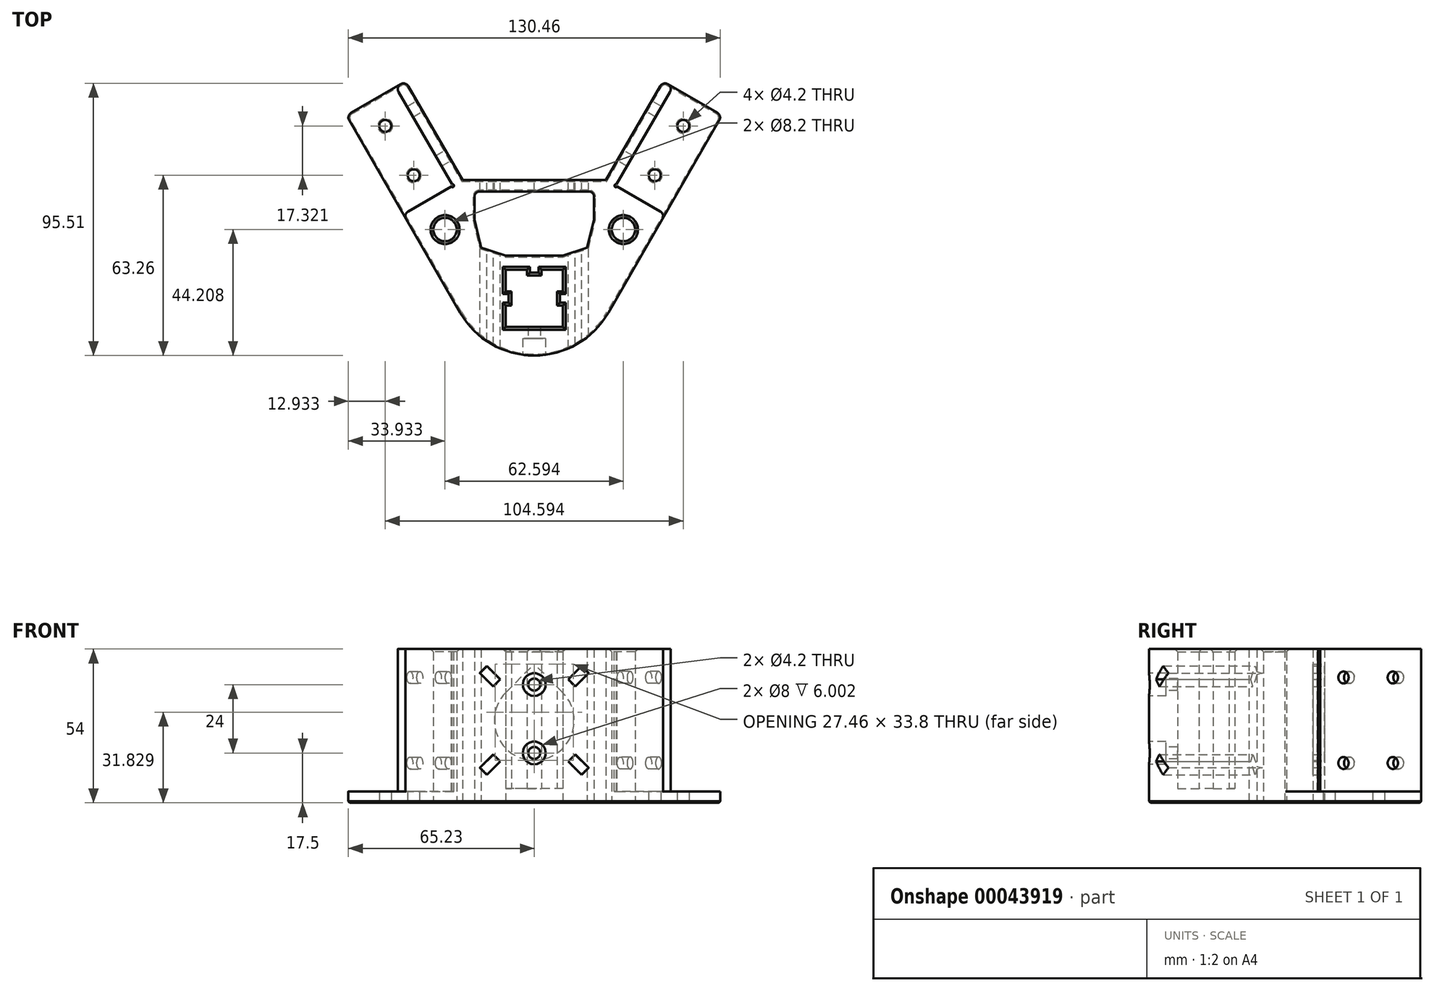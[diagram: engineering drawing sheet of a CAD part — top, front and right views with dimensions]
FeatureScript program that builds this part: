
annotation { "Feature Type Name" : "Feature", "Feature Type Description" : "" }
export const myFeature = defineFeature(function(context is Context, id is Id, definition is map)
    precondition{}
    {
        {
            var Q0;
            Q0=qCreatedBy(makeId("Top.planeOp"),FACE);
            var sketch = newSketch(context, id + "F0", { "sketchPlane" : qUnion([Q0])});
            skLineSegment(sketch, "E0.rect.bottom", {"start": v(10.05, -10.05) * mm, "end": v(-10.05, -10.05) * mm});
            skLineSegment(sketch, "E0.rect.top", {"start": v(10.05, 10.05) * mm, "end": v(-10.05, 10.05) * mm});
            skLineSegment(sketch, "E0.rect.left", {"start": v(10.05, -10.05) * mm, "end": v(10.05, 10.05) * mm});
            skLineSegment(sketch, "E0.rect.right", {"start": v(-10.05, -10.05) * mm, "end": v(-10.05, 10.05) * mm});
            skPoint(sketch, "E0.rect.middle", {"position": v(0, 0) * mm});
            skLineSegment(sketch, "E1", {"start": v(-10.05, -2.5) * mm, "end": v(-8.05, -2.5) * mm});
            skLineSegment(sketch, "E2", {"start": v(-8.05, -2.5) * mm, "end": v(-8.05, 2.5) * mm});
            skLineSegment(sketch, "E3", {"start": v(-8.05, 2.5) * mm, "end": v(-10.05, 2.5) * mm});
            skLineSegment(sketch, "E4", {"start": v(-2.5, 10.05) * mm, "end": v(-2.5, 8.05) * mm});
            skLineSegment(sketch, "E5", {"start": v(-2.5, 8.05) * mm, "end": v(2.5, 8.05) * mm});
            skLineSegment(sketch, "E6", {"start": v(2.5, 8.05) * mm, "end": v(2.5, 10.05) * mm});
            skLineSegment(sketch, "E7", {"start": v(10.05, 2.5) * mm, "end": v(8.05, 2.5) * mm});
            skLineSegment(sketch, "E8", {"start": v(8.05, 2.5) * mm, "end": v(8.05, -2.5) * mm});
            skLineSegment(sketch, "E9", {"start": v(8.05, -2.5) * mm, "end": v(10.05, -2.5) * mm});
            skLineSegment(sketch, "E10", {"start": v(-25.98, -5.05) * mm, "end": v(-65.96, 64.2) * mm});
            skLineSegment(sketch, "E11", {"start": v(-65.96, 64.2) * mm, "end": v(-45.17, 76.2) * mm});
            skLineSegment(sketch, "E12", {"start": v(-45.17, 76.2) * mm, "end": v(-25.17, 41.55) * mm});
            skLineSegment(sketch, "E13", {"start": v(-25.17, 41.55) * mm, "end": v(25.17, 41.55) * mm});
            skLineSegment(sketch, "E14", {"start": v(25.17, 41.55) * mm, "end": v(45.17, 76.2) * mm});
            skLineSegment(sketch, "E15", {"start": v(45.17, 76.2) * mm, "end": v(65.96, 64.2) * mm});
            skLineSegment(sketch, "E16", {"start": v(65.96, 64.2) * mm, "end": v(25.98, -5.05) * mm});
            skPoint(sketch, "E17.visualSharp", {"position": v(0, -50.05) * mm});
            skArc(sketch, "E17.filletArc", {"start": v(-25.98, -5.05) * mm, "mid": v(0, -20.05) * mm, "end": v(25.98, -5.05) * mm});
            skLineSegment(sketch, "E18", {"start": v(-48.64, 74.2) * mm, "end": v(-28.64, 39.55) * mm});
            skLineSegment(sketch, "E19", {"start": v(-28.64, 39.55) * mm, "end": v(-45.96, 29.55) * mm});
            skLineSegment(sketch, "E20", {"start": v(48.64, 74.2) * mm, "end": v(28.64, 39.55) * mm});
            skLineSegment(sketch, "E21", {"start": v(28.64, 39.55) * mm, "end": v(45.96, 29.55) * mm});
            skLineSegment(sketch, "E22", {"start": v(-28.64, 39.55) * mm, "end": v(-25.17, 41.55) * mm, "construction": true});
            skLineSegment(sketch, "E23", {"start": v(-57.3, 69.2) * mm, "end": v(-37.3, 34.55) * mm, "construction": true});
            skCircle(sketch, "E24", {"center": v(-52.3, 60.53) * mm, "radius": 2.1 * mm});
            skCircle(sketch, "E25", {"center": v(-42.3, 43.21) * mm, "radius": 2.1 * mm});
            skCircle(sketch, "E26", {"center": v(52.3, 60.53) * mm, "radius": 2.1 * mm});
            skCircle(sketch, "E27", {"center": v(42.3, 43.21) * mm, "radius": 2.1 * mm});
            skLineSegment(sketch, "E28", {"start": v(-21, 37.55) * mm, "end": v(21, 37.55) * mm});
            skLineSegment(sketch, "E29", {"start": v(21, 37.55) * mm, "end": v(21, 27.55) * mm});
            skLineSegment(sketch, "E30", {"start": v(10.05, 15.05) * mm, "end": v(-10.05, 15.05) * mm});
            skLineSegment(sketch, "E31", {"start": v(-21, 27.55) * mm, "end": v(-21, 37.55) * mm});
            skLineSegment(sketch, "E32", {"start": v(-21, 27.55) * mm, "end": v(-18.6, 17.84) * mm});
            skLineSegment(sketch, "E33", {"start": v(-18.6, 17.84) * mm, "end": v(-10.05, 15.05) * mm});
            skLineSegment(sketch, "E34", {"start": v(21, 27.55) * mm, "end": v(18.6, 17.84) * mm});
            skLineSegment(sketch, "E35", {"start": v(18.6, 17.84) * mm, "end": v(10.05, 15.05) * mm});
            skLineSegment(sketch, "E36", {"start": v(-37.3, 34.55) * mm, "end": v(-20.56, 5.56) * mm, "construction": true});
            skCircle(sketch, "E37", {"center": v(-31.3, 24.16) * mm, "radius": 4.1 * mm});
            skLineSegment(sketch, "E38", {"start": v(0, -71.13) * mm, "end": v(0, 233.1) * mm, "construction": true});
            skCircle(sketch, "E39", {"center": v(31.3, 24.16) * mm, "radius": 4.1 * mm});
            skSolve(sketch);
        }
        {
            var Q0;
            {var subQ5=sQuery(id+"F0.wireOp",EDGE,"E0.rect.bottom");Q0=makeQuery(id+"F0.imprint","IMPRINT",FACE,{"disambiguationData":[TD([[makeQuery(id+"F0.imprint","IMPRINT",EDGE,{"derivedFrom":subQ5}),1.0]])]});}
            var Q1;
            {var subQ1=sQuery(id+"F0.wireOp",EDGE,"E18");Q1=makeQuery(id+"F0.imprint","IMPRINT",FACE,{"disambiguationData":[TD([[makeQuery(id+"F0.imprint","IMPRINT",EDGE,{"derivedFrom":subQ1}),-1.0]])]});}
            var Q2;
            {var subQ0=sQuery(id+"F0.wireOp",EDGE,"E20");Q2=makeQuery(id+"F0.imprint","IMPRINT",FACE,{"disambiguationData":[TD([[makeQuery(id+"F0.imprint","IMPRINT",EDGE,{"derivedFrom":subQ0}),1.0]])]});}
            var Q3;
            {var subQ1=sQuery(id+"F0.wireOp",EDGE,"E1");Q3=makeQuery(id+"F0.imprint","IMPRINT",FACE,{"disambiguationData":[TD([[makeQuery(id+"F0.imprint","IMPRINT",EDGE,{"derivedFrom":subQ1}),1.0]])]});}
            var Q4;
            {var subQ1=sQuery(id+"F0.wireOp",EDGE,"E4");Q4=makeQuery(id+"F0.imprint","IMPRINT",FACE,{"disambiguationData":[TD([[makeQuery(id+"F0.imprint","IMPRINT",EDGE,{"derivedFrom":subQ1}),1.0]])]});}
            var Q5;
            {var subQ1=sQuery(id+"F0.wireOp",EDGE,"E7");Q5=makeQuery(id+"F0.imprint","IMPRINT",FACE,{"disambiguationData":[TD([[makeQuery(id+"F0.imprint","IMPRINT",EDGE,{"derivedFrom":subQ1}),1.0]])]});}
            extrude(context, id + "F1", {"entities" : qUnion([Q0, Q1, Q2, Q3, Q4, Q5]), "depth" : 4 * mm});
        }
        {
            var Q0;
            Q0=makeQuery(id+"F1.opExtrude","CAP_FACE",FACE,{"disambiguationData":[OSD([sQuery(id+"F0.wireOp",EDGE,"E0.rect.bottom"),sQuery(id+"F0.wireOp",EDGE,"E0.rect.top"),sQuery(id+"F0.wireOp",EDGE,"E0.rect.left"),sQuery(id+"F0.wireOp",EDGE,"E0.rect.right"),sQuery(id+"F0.wireOp",EDGE,"E1"),sQuery(id+"F0.wireOp",EDGE,"E2"),sQuery(id+"F0.wireOp",EDGE,"E3"),sQuery(id+"F0.wireOp",EDGE,"E4"),sQuery(id+"F0.wireOp",EDGE,"E5"),sQuery(id+"F0.wireOp",EDGE,"E6"),sQuery(id+"F0.wireOp",EDGE,"E7"),sQuery(id+"F0.wireOp",EDGE,"E8"),sQuery(id+"F0.wireOp",EDGE,"E9"),sQuery(id+"F0.wireOp",EDGE,"E10"),sQuery(id+"F0.wireOp",EDGE,"E11"),sQuery(id+"F0.wireOp",EDGE,"E12"),sQuery(id+"F0.wireOp",EDGE,"E13"),sQuery(id+"F0.wireOp",EDGE,"E14"),sQuery(id+"F0.wireOp",EDGE,"E15"),sQuery(id+"F0.wireOp",EDGE,"E16"),sQuery(id+"F0.wireOp",EDGE,"E17.filletArc"),sQuery(id+"F0.wireOp",EDGE,"E24"),sQuery(id+"F0.wireOp",EDGE,"E25"),sQuery(id+"F0.wireOp",EDGE,"E26"),sQuery(id+"F0.wireOp",EDGE,"E27"),sQuery(id+"F0.wireOp",EDGE,"E28"),sQuery(id+"F0.wireOp",EDGE,"E29"),sQuery(id+"F0.wireOp",EDGE,"E30"),sQuery(id+"F0.wireOp",EDGE,"E31"),sQuery(id+"F0.wireOp",EDGE,"E32"),sQuery(id+"F0.wireOp",EDGE,"E33"),sQuery(id+"F0.wireOp",EDGE,"E34"),sQuery(id+"F0.wireOp",EDGE,"E35"),sQuery(id+"F0.wireOp",EDGE,"E37"),sQuery(id+"F0.wireOp",EDGE,"E39")])],"isStart":false});
            var sketch = newSketch(context, id + "F2", { "sketchPlane" : qUnion([Q0])});
            skLineSegment(sketch, "E40.0", {"start": v(-48.64, 74.2) * mm, "end": v(-28.64, 39.55) * mm});
            skLineSegment(sketch, "E41.0", {"start": v(-28.64, 39.55) * mm, "end": v(-45.96, 29.55) * mm});
            skLineSegment(sketch, "E42.0", {"start": v(48.64, 74.2) * mm, "end": v(28.64, 39.55) * mm});
            skLineSegment(sketch, "E43.0", {"start": v(28.64, 39.55) * mm, "end": v(45.96, 29.55) * mm});
            skSolve(sketch);
        }
        {
            var Q0;
            {var subQ7=sQuery(id+"F2.wireOp",EDGE,"E40.0");Q0=makeQuery(id+"F2.imprint","IMPRINT",FACE,{"disambiguationData":[TD([[makeQuery(id+"F2.imprint","IMPRINT",EDGE,{"derivedFrom":subQ7}),1.0]])]});}
            extrude(context, id + "F3", {"entities" : qUnion([Q0]), "operationType" : NewBodyOperationType.ADD, "depth" : 50 * mm});
        }
        {
            var Q0;
            {var subQ0=sQuery(id+"F0.wireOp",EDGE,"E13");Q0=makeQuery(id+"F3.boolean.opBoolean","MERGE",FACE,{"derivedFrom":[makeQuery(id+"F1.opExtrude","SWEPT_FACE",FACE,{"disambiguationData":[OSD([subQ0])]}),makeQuery(id+"F3.opExtrude","SWEPT_FACE",FACE,{"disambiguationData":[OSD([subQ0])]})]});}
            var sketch = newSketch(context, id + "F4", { "sketchPlane" : qUnion([Q0])});
            skCircle(sketch, "E44", {"center": v(0, 28.93) * mm, "radius": 14 * mm});
            skLineSegment(sketch, "E45", {"start": v(0, 28.93) * mm, "end": v(-14.76, 43.7) * mm, "construction": true});
            skLineSegment(sketch, "E46", {"start": v(-19.07, 45.53) * mm, "end": v(-16.6, 48) * mm});
            skLineSegment(sketch, "E47", {"start": v(-16.6, 48) * mm, "end": v(-11.93, 43.33) * mm});
            skLineSegment(sketch, "E48", {"start": v(-11.93, 43.33) * mm, "end": v(-14.4, 40.86) * mm});
            skLineSegment(sketch, "E49", {"start": v(-14.4, 40.86) * mm, "end": v(-19.07, 45.53) * mm});
            skLineSegment(sketch, "E50.1.0", {"start": v(-11.93, 14.53) * mm, "end": v(-16.6, 9.86) * mm});
            skLineSegment(sketch, "E50.1.1", {"start": v(-16.6, 9.86) * mm, "end": v(-19.07, 12.33) * mm});
            skLineSegment(sketch, "E50.1.2", {"start": v(-19.07, 12.33) * mm, "end": v(-14.4, 17) * mm});
            skLineSegment(sketch, "E50.1.3", {"start": v(-14.4, 17) * mm, "end": v(-11.93, 14.53) * mm});
            skLineSegment(sketch, "E50.2.0", {"start": v(14.4, 17) * mm, "end": v(19.07, 12.33) * mm});
            skLineSegment(sketch, "E50.2.1", {"start": v(19.07, 12.33) * mm, "end": v(16.6, 9.86) * mm});
            skLineSegment(sketch, "E50.2.2", {"start": v(16.6, 9.86) * mm, "end": v(11.93, 14.53) * mm});
            skLineSegment(sketch, "E50.2.3", {"start": v(11.93, 14.53) * mm, "end": v(14.4, 17) * mm});
            skLineSegment(sketch, "E50.3.0", {"start": v(11.93, 43.33) * mm, "end": v(16.6, 48) * mm});
            skLineSegment(sketch, "E50.3.1", {"start": v(16.6, 48) * mm, "end": v(19.07, 45.53) * mm});
            skLineSegment(sketch, "E50.3.2", {"start": v(19.07, 45.53) * mm, "end": v(14.4, 40.86) * mm});
            skLineSegment(sketch, "E50.3.3", {"start": v(14.4, 40.86) * mm, "end": v(11.93, 43.33) * mm});
            skLineSegment(sketch, "E51", {"start": v(0, 48.73) * mm, "end": v(-9.9, 38.83) * mm});
            skLineSegment(sketch, "E52", {"start": v(0, 48.73) * mm, "end": v(9.9, 38.83) * mm});
            skSolve(sketch);
        }
        {
            var Q0;
            Q0=makeQuery(id+"F4.imprint","IMPRINT",FACE,{"disambiguationData":[TD([[makeQuery(id+"F4.imprint","IMPRINT",EDGE,{"derivedFrom":sQuery(id+"F4.wireOp",EDGE,"E44")}),1.0]])]});
            var Q1;
            {var subQ1=sQuery(id+"F4.wireOp",EDGE,"E51");Q1=makeQuery(id+"F4.imprint","IMPRINT",FACE,{"disambiguationData":[TD([[makeQuery(id+"F4.imprint","IMPRINT",EDGE,{"derivedFrom":subQ1}),1.0]])]});}
            extrude(context, id + "F5", {"entities" : qUnion([Q0, Q1]), "operationType" : NewBodyOperationType.REMOVE, "endBound" : BoundingType.UP_TO_NEXT, "oppositeDirection" : true, "depth" : 25 * mm});
        }
        {
            var Q0;
            Q0=makeQuery(id+"F4.imprint","IMPRINT",FACE,{"disambiguationData":[TD([[makeQuery(id+"F4.imprint","IMPRINT",EDGE,{"derivedFrom":sQuery(id+"F4.wireOp",EDGE,"E46")}),-1.0]])]});
            var Q1;
            Q1=makeQuery(id+"F4.imprint","IMPRINT",FACE,{"disambiguationData":[TD([[makeQuery(id+"F4.imprint","IMPRINT",EDGE,{"derivedFrom":sQuery(id+"F4.wireOp",EDGE,"E50.3.0")}),-1.0]])]});
            var Q2;
            Q2=makeQuery(id+"F4.imprint","IMPRINT",FACE,{"disambiguationData":[TD([[makeQuery(id+"F4.imprint","IMPRINT",EDGE,{"derivedFrom":sQuery(id+"F4.wireOp",EDGE,"E50.2.0")}),-1.0]])]});
            var Q3;
            Q3=makeQuery(id+"F4.imprint","IMPRINT",FACE,{"disambiguationData":[TD([[makeQuery(id+"F4.imprint","IMPRINT",EDGE,{"derivedFrom":sQuery(id+"F4.wireOp",EDGE,"E50.1.0")}),-1.0]])]});
            extrude(context, id + "F6", {"entities" : qUnion([Q0, Q1, Q2, Q3]), "operationType" : NewBodyOperationType.REMOVE, "endBound" : BoundingType.THROUGH_ALL, "oppositeDirection" : true, "depth" : 25 * mm});
        }
        {
            var Q0;
            {var subQ11=sQuery(id+"F0.wireOp",EDGE,"E0.rect.bottom");Q0=makeQuery(id+"F0.imprint","IMPRINT",FACE,{"disambiguationData":[TD([[makeQuery(id+"F0.imprint","IMPRINT",EDGE,{"derivedFrom":subQ11}),-1.0]])]});}
            extrude(context, id + "F7", {"entities" : qUnion([Q0]), "operationType" : NewBodyOperationType.ADD, "depth" : 5 * mm});
        }
        {
            var Q0;
            {var subQ0=sQuery(id+"F0.wireOp",EDGE,"E28");Q0=makeQuery(id+"F3.boolean.opBoolean","MERGE",FACE,{"derivedFrom":[makeQuery(id+"F1.opExtrude","SWEPT_FACE",FACE,{"disambiguationData":[OSD([subQ0])]}),makeQuery(id+"F3.opExtrude","SWEPT_FACE",FACE,{"disambiguationData":[OSD([subQ0])]})]});}
            cPlane(context, id + "F8", {"entities" : qUnion([Q0]), "cplaneType" : CPlaneType.OFFSET, "offset" : 100 * mm, "width" : 150 * mm, "height" : 150 * mm});
        }
        {
            var Q0;
            Q0=qCreatedBy(id+"F8.planeOp",FACE);
            var sketch = newSketch(context, id + "F9", { "sketchPlane" : qUnion([Q0])});
            skCircle(sketch, "E53", {"center": v(0, 41.5) * mm, "radius": 2.1 * mm});
            skCircle(sketch, "E54", {"center": v(0, 41.5) * mm, "radius": 4 * mm});
            skCircle(sketch, "E55", {"center": v(0, 17.5) * mm, "radius": 2.1 * mm});
            skCircle(sketch, "E56", {"center": v(0, 17.5) * mm, "radius": 4 * mm});
            skSolve(sketch);
        }
        {
            var Q0;
            Q0=makeQuery(id+"F9.imprint","IMPRINT",FACE,{"disambiguationData":[TD([[makeQuery(id+"F9.imprint","IMPRINT",EDGE,{"derivedFrom":sQuery(id+"F9.wireOp",EDGE,"E53")}),1.0]])]});
            var Q1;
            Q1=makeQuery(id+"F9.imprint","IMPRINT",FACE,{"disambiguationData":[TD([[makeQuery(id+"F9.imprint","IMPRINT",EDGE,{"derivedFrom":sQuery(id+"F9.wireOp",EDGE,"E55")}),1.0]])]});
            var Q2;
            {var subQ0=sQuery(id+"F0.wireOp",EDGE,"E0.rect.bottom");Q2=makeQuery(id+"F3.boolean.opBoolean","MERGE",FACE,{"derivedFrom":[makeQuery(id+"F1.opExtrude","SWEPT_FACE",FACE,{"disambiguationData":[OSD([subQ0])]}),makeQuery(id+"F3.opExtrude","SWEPT_FACE",FACE,{"disambiguationData":[OSD([subQ0])]})]});}
            extrude(context, id + "F10", {"entities" : qUnion([Q0, Q1]), "operationType" : NewBodyOperationType.REMOVE, "endBound" : BoundingType.UP_TO_SURFACE, "oppositeDirection" : true, "endBoundEntityFace" : qUnion([Q2]), "depth" : 25 * mm});
        }
        {
            var Q0;
            Q0=makeQuery(id+"F9.imprint","IMPRINT",FACE,{"disambiguationData":[TD([[makeQuery(id+"F9.imprint","IMPRINT",EDGE,{"derivedFrom":sQuery(id+"F9.wireOp",EDGE,"E53")}),-1.0]])]});
            var Q1;
            Q1=makeQuery(id+"F9.imprint","IMPRINT",FACE,{"disambiguationData":[TD([[makeQuery(id+"F9.imprint","IMPRINT",EDGE,{"derivedFrom":sQuery(id+"F9.wireOp",EDGE,"E55")}),-1.0]])]});
            extrude(context, id + "F11", {"entities" : qUnion([Q0, Q1]), "operationType" : NewBodyOperationType.REMOVE, "oppositeDirection" : true, "depth" : 48.4 * mm});
        }
        {
            var Q0;
            {var subQ0=sQuery(id+"F0.wireOp",EDGE,"E12");Q0=makeQuery(id+"F3.boolean.opBoolean","MERGE",FACE,{"derivedFrom":[makeQuery(id+"F1.opExtrude","SWEPT_FACE",FACE,{"disambiguationData":[OSD([subQ0])]}),makeQuery(id+"F3.opExtrude","SWEPT_FACE",FACE,{"disambiguationData":[OSD([subQ0])]})]});}
            var sketch = newSketch(context, id + "F12", { "sketchPlane" : qUnion([Q0])});
            skCircle(sketch, "E57", {"center": v(78.57, 44) * mm, "radius": 2.1 * mm});
            skCircle(sketch, "E58", {"center": v(58.57, 44) * mm, "radius": 2.1 * mm});
            skCircle(sketch, "E59", {"center": v(78.57, 14) * mm, "radius": 2.1 * mm});
            skCircle(sketch, "E60", {"center": v(58.57, 14) * mm, "radius": 2.1 * mm});
            skSolve(sketch);
        }
        {
            var Q0;
            Q0=qSketchRegion(id+"F12",true);
            extrude(context, id + "F13", {"entities" : qUnion([Q0]), "operationType" : NewBodyOperationType.REMOVE, "oppositeDirection" : true, "depth" : 25 * mm});
        }
        {
            var Q0;
            {var subQ0=sQuery(id+"F0.wireOp",EDGE,"E14");Q0=makeQuery(id+"F3.boolean.opBoolean","MERGE",FACE,{"derivedFrom":[makeQuery(id+"F1.opExtrude","SWEPT_FACE",FACE,{"disambiguationData":[OSD([subQ0])]}),makeQuery(id+"F3.opExtrude","SWEPT_FACE",FACE,{"disambiguationData":[OSD([subQ0])]})]});}
            var sketch = newSketch(context, id + "F14", { "sketchPlane" : qUnion([Q0])});
            skCircle(sketch, "E61", {"center": v(-78.57, 44) * mm, "radius": 2.1 * mm});
            skCircle(sketch, "E62", {"center": v(-58.57, 44) * mm, "radius": 2.1 * mm});
            skCircle(sketch, "E63", {"center": v(-78.57, 14) * mm, "radius": 2.1 * mm});
            skCircle(sketch, "E64", {"center": v(-58.57, 14) * mm, "radius": 2.1 * mm});
            skSolve(sketch);
        }
        {
            var Q0;
            Q0=qSketchRegion(id+"F14",true);
            extrude(context, id + "F15", {"entities" : qUnion([Q0]), "operationType" : NewBodyOperationType.REMOVE, "oppositeDirection" : true, "depth" : 25 * mm});
        }
        {
            var Q0;
            Q0=makeQuery(id+"F3.opExtrude","CAP_EDGE",EDGE,{"disambiguationData":[OSD([sQuery(id+"F0.wireOp",EDGE,"E0.rect.bottom")])],"isStart":false});
            var Q1;
            {var subQ0=sQuery(id+"F0.wireOp",EDGE,"E0.rect.left");Q1=makeQuery(id+"F3.opExtrude","CAP_EDGE",EDGE,{"disambiguationData":[OSD([subQ0]),TDD([makeQuery(id+"F2.imprint","IMPRINT",EDGE,{"derivedFrom":makeQuery(id+"F1.opExtrude","CAP_EDGE",EDGE,{"disambiguationData":[OSD([subQ0]),TDD([makeQuery(id+"F0.imprint","IMPRINT",EDGE,{"disambiguationData":[TD([[makeQuery(id+"F0.imprint","INTERSECT",VERTEX,{"derivedFrom":[sQuery(id+"F0.wireOp",EDGE,"E0.rect.bottom"),subQ0]}),-1.0]])],"derivedFrom":subQ0})])],"isStart":false})})])],"isStart":false});}
            var Q2;
            Q2=makeQuery(id+"F3.opExtrude","CAP_EDGE",EDGE,{"disambiguationData":[OSD([sQuery(id+"F0.wireOp",EDGE,"E9")])],"isStart":false});
            var Q3;
            Q3=makeQuery(id+"F3.opExtrude","CAP_EDGE",EDGE,{"disambiguationData":[OSD([sQuery(id+"F0.wireOp",EDGE,"E8")])],"isStart":false});
            var Q4;
            Q4=makeQuery(id+"F3.opExtrude","CAP_EDGE",EDGE,{"disambiguationData":[OSD([sQuery(id+"F0.wireOp",EDGE,"E7")])],"isStart":false});
            var Q5;
            {var subQ0=sQuery(id+"F0.wireOp",EDGE,"E0.rect.left");Q5=makeQuery(id+"F3.opExtrude","CAP_EDGE",EDGE,{"disambiguationData":[OSD([subQ0]),TDD([makeQuery(id+"F2.imprint","IMPRINT",EDGE,{"derivedFrom":makeQuery(id+"F1.opExtrude","CAP_EDGE",EDGE,{"disambiguationData":[OSD([subQ0]),TDD([makeQuery(id+"F0.imprint","IMPRINT",EDGE,{"disambiguationData":[TD([[makeQuery(id+"F0.imprint","INTERSECT",VERTEX,{"derivedFrom":[sQuery(id+"F0.wireOp",EDGE,"E0.rect.top"),subQ0]}),1.0]])],"derivedFrom":subQ0})])],"isStart":false})})])],"isStart":false});}
            var Q6;
            {var subQ0=sQuery(id+"F0.wireOp",EDGE,"E0.rect.top");Q6=makeQuery(id+"F3.opExtrude","CAP_EDGE",EDGE,{"disambiguationData":[OSD([subQ0]),TDD([makeQuery(id+"F2.imprint","IMPRINT",EDGE,{"derivedFrom":makeQuery(id+"F1.opExtrude","CAP_EDGE",EDGE,{"disambiguationData":[OSD([subQ0]),TDD([makeQuery(id+"F0.imprint","IMPRINT",EDGE,{"disambiguationData":[TD([[makeQuery(id+"F0.imprint","INTERSECT",VERTEX,{"derivedFrom":[subQ0,sQuery(id+"F0.wireOp",EDGE,"E0.rect.left")]}),-1.0]])],"derivedFrom":subQ0})])],"isStart":false})})])],"isStart":false});}
            var Q7;
            Q7=makeQuery(id+"F3.opExtrude","CAP_EDGE",EDGE,{"disambiguationData":[OSD([sQuery(id+"F0.wireOp",EDGE,"E6")])],"isStart":false});
            var Q8;
            Q8=makeQuery(id+"F3.opExtrude","CAP_EDGE",EDGE,{"disambiguationData":[OSD([sQuery(id+"F0.wireOp",EDGE,"E5")])],"isStart":false});
            var Q9;
            Q9=makeQuery(id+"F3.opExtrude","CAP_EDGE",EDGE,{"disambiguationData":[OSD([sQuery(id+"F0.wireOp",EDGE,"E4")])],"isStart":false});
            var Q10;
            {var subQ0=sQuery(id+"F0.wireOp",EDGE,"E0.rect.top");Q10=makeQuery(id+"F3.opExtrude","CAP_EDGE",EDGE,{"disambiguationData":[OSD([subQ0]),TDD([makeQuery(id+"F2.imprint","IMPRINT",EDGE,{"derivedFrom":makeQuery(id+"F1.opExtrude","CAP_EDGE",EDGE,{"disambiguationData":[OSD([subQ0]),TDD([makeQuery(id+"F0.imprint","IMPRINT",EDGE,{"disambiguationData":[TD([[makeQuery(id+"F0.imprint","INTERSECT",VERTEX,{"derivedFrom":[subQ0,sQuery(id+"F0.wireOp",EDGE,"E0.rect.right")]}),1.0]])],"derivedFrom":subQ0})])],"isStart":false})})])],"isStart":false});}
            var Q11;
            {var subQ0=sQuery(id+"F0.wireOp",EDGE,"E0.rect.right");Q11=makeQuery(id+"F3.opExtrude","CAP_EDGE",EDGE,{"disambiguationData":[OSD([subQ0]),TDD([makeQuery(id+"F2.imprint","IMPRINT",EDGE,{"derivedFrom":makeQuery(id+"F1.opExtrude","CAP_EDGE",EDGE,{"disambiguationData":[OSD([subQ0]),TDD([makeQuery(id+"F0.imprint","IMPRINT",EDGE,{"disambiguationData":[TD([[makeQuery(id+"F0.imprint","INTERSECT",VERTEX,{"derivedFrom":[sQuery(id+"F0.wireOp",EDGE,"E0.rect.top"),subQ0]}),1.0]])],"derivedFrom":subQ0})])],"isStart":false})})])],"isStart":false});}
            var Q12;
            Q12=makeQuery(id+"F3.opExtrude","CAP_EDGE",EDGE,{"disambiguationData":[OSD([sQuery(id+"F0.wireOp",EDGE,"E3")])],"isStart":false});
            var Q13;
            Q13=makeQuery(id+"F3.opExtrude","CAP_EDGE",EDGE,{"disambiguationData":[OSD([sQuery(id+"F0.wireOp",EDGE,"E2")])],"isStart":false});
            var Q14;
            Q14=makeQuery(id+"F3.opExtrude","CAP_EDGE",EDGE,{"disambiguationData":[OSD([sQuery(id+"F0.wireOp",EDGE,"E1")])],"isStart":false});
            var Q15;
            {var subQ0=sQuery(id+"F0.wireOp",EDGE,"E0.rect.right");Q15=makeQuery(id+"F3.opExtrude","CAP_EDGE",EDGE,{"disambiguationData":[OSD([subQ0]),TDD([makeQuery(id+"F2.imprint","IMPRINT",EDGE,{"derivedFrom":makeQuery(id+"F1.opExtrude","CAP_EDGE",EDGE,{"disambiguationData":[OSD([subQ0]),TDD([makeQuery(id+"F0.imprint","IMPRINT",EDGE,{"disambiguationData":[TD([[makeQuery(id+"F0.imprint","INTERSECT",VERTEX,{"derivedFrom":[sQuery(id+"F0.wireOp",EDGE,"E0.rect.bottom"),subQ0]}),-1.0]])],"derivedFrom":subQ0})])],"isStart":false})})])],"isStart":false});}
            var Q16;
            Q16=makeQuery(id+"F3.opExtrude","CAP_EDGE",EDGE,{"disambiguationData":[OSD([sQuery(id+"F0.wireOp",EDGE,"E39")])],"isStart":false});
            var Q17;
            Q17=makeQuery(id+"F3.opExtrude","CAP_EDGE",EDGE,{"disambiguationData":[OSD([sQuery(id+"F0.wireOp",EDGE,"E37")])],"isStart":false});
            chamfer(context, id + "F16", {"entities" : qUnion([Q0, Q1, Q2, Q3, Q4, Q5, Q6, Q7, Q8, Q9, Q10, Q11, Q12, Q13, Q14, Q15, Q16, Q17]), "width" : 1 * mm, "tangentPropagation" : true});
        }
        {
            var Q0;
            Q0=makeQuery(id+"F3.opExtrude","CAP_FACE",FACE,{"disambiguationData":[OSD([sQuery(id+"F0.wireOp",EDGE,"E0.rect.bottom"),sQuery(id+"F0.wireOp",EDGE,"E0.rect.top"),sQuery(id+"F0.wireOp",EDGE,"E0.rect.left"),sQuery(id+"F0.wireOp",EDGE,"E0.rect.right"),sQuery(id+"F0.wireOp",EDGE,"E1"),sQuery(id+"F0.wireOp",EDGE,"E2"),sQuery(id+"F0.wireOp",EDGE,"E3"),sQuery(id+"F0.wireOp",EDGE,"E4"),sQuery(id+"F0.wireOp",EDGE,"E5"),sQuery(id+"F0.wireOp",EDGE,"E6"),sQuery(id+"F0.wireOp",EDGE,"E7"),sQuery(id+"F0.wireOp",EDGE,"E8"),sQuery(id+"F0.wireOp",EDGE,"E9"),sQuery(id+"F0.wireOp",EDGE,"E10"),sQuery(id+"F0.wireOp",EDGE,"E11"),sQuery(id+"F0.wireOp",EDGE,"E12"),sQuery(id+"F0.wireOp",EDGE,"E13"),sQuery(id+"F0.wireOp",EDGE,"E14"),sQuery(id+"F0.wireOp",EDGE,"E15"),sQuery(id+"F0.wireOp",EDGE,"E16"),sQuery(id+"F0.wireOp",EDGE,"E17.filletArc"),sQuery(id+"F0.wireOp",EDGE,"E28"),sQuery(id+"F0.wireOp",EDGE,"E29"),sQuery(id+"F0.wireOp",EDGE,"E30"),sQuery(id+"F0.wireOp",EDGE,"E31"),sQuery(id+"F0.wireOp",EDGE,"E32"),sQuery(id+"F0.wireOp",EDGE,"E33"),sQuery(id+"F0.wireOp",EDGE,"E34"),sQuery(id+"F0.wireOp",EDGE,"E35"),sQuery(id+"F0.wireOp",EDGE,"E37"),sQuery(id+"F0.wireOp",EDGE,"E39"),sQuery(id+"F2.wireOp",EDGE,"E40.0"),sQuery(id+"F2.wireOp",EDGE,"E41.0"),sQuery(id+"F2.wireOp",EDGE,"E42.0"),sQuery(id+"F2.wireOp",EDGE,"E43.0")])],"isStart":false});
            var sketch = newSketch(context, id + "F17", { "sketchPlane" : qUnion([Q0])});
            skCircle(sketch, "E65", {"center": v(-28.64, 39.55) * mm, "radius": 0.5 * mm});
            skCircle(sketch, "E66", {"center": v(28.64, 39.55) * mm, "radius": 0.5 * mm});
            skSolve(sketch);
        }
        {
            var Q0;
            {var subQ1=sQuery(id+"F17.wireOp",EDGE,"E65");var subQ3=makeQuery(id+"F3.opExtrude","CAP_EDGE",EDGE,{"disambiguationData":[OSD([sQuery(id+"F2.wireOp",EDGE,"E40.0")])],"isStart":false});var subQ5=makeQuery(id+"F17.imprint","INTERSECT",VERTEX,{"derivedFrom":[subQ3,subQ1]});Q0=makeQuery(id+"F17.imprint","IMPRINT",FACE,{"disambiguationData":[TD([[makeQuery(id+"F17.imprint","IMPRINT",EDGE,{"disambiguationData":[TD([[subQ5,1.0]])],"derivedFrom":subQ1}),1.0]])]});}
            var Q1;
            {var subQ1=sQuery(id+"F17.wireOp",EDGE,"E66");var subQ3=makeQuery(id+"F3.opExtrude","CAP_EDGE",EDGE,{"disambiguationData":[OSD([sQuery(id+"F2.wireOp",EDGE,"E42.0")])],"isStart":false});var subQ5=makeQuery(id+"F17.imprint","INTERSECT",VERTEX,{"derivedFrom":[subQ3,subQ1]});Q1=makeQuery(id+"F17.imprint","IMPRINT",FACE,{"disambiguationData":[TD([[makeQuery(id+"F17.imprint","IMPRINT",EDGE,{"disambiguationData":[TD([[subQ5,-1.0]])],"derivedFrom":subQ1}),1.0]])]});}
            var Q2;
            {var subQ0=sQuery(id+"F0.wireOp",EDGE,"E10");var subQ1=sQuery(id+"F0.wireOp",EDGE,"E11");var subQ2=sQuery(id+"F0.wireOp",EDGE,"E24");var subQ3=sQuery(id+"F0.wireOp",EDGE,"E25");Q2=makeQuery(id+"F3.boolean.opBoolean","SPLIT",FACE,{"disambiguationData":[TD([makeQuery(id+"F1.opExtrude","SWEPT_FACE",FACE,{"disambiguationData":[OSD([subQ0])]})])],"derivedFrom":makeQuery(id+"F1.opExtrude","CAP_FACE",FACE,{"disambiguationData":[OSD([sQuery(id+"F0.wireOp",EDGE,"E0.rect.bottom"),sQuery(id+"F0.wireOp",EDGE,"E0.rect.top"),sQuery(id+"F0.wireOp",EDGE,"E0.rect.left"),sQuery(id+"F0.wireOp",EDGE,"E0.rect.right"),sQuery(id+"F0.wireOp",EDGE,"E1"),sQuery(id+"F0.wireOp",EDGE,"E2"),sQuery(id+"F0.wireOp",EDGE,"E3"),sQuery(id+"F0.wireOp",EDGE,"E4"),sQuery(id+"F0.wireOp",EDGE,"E5"),sQuery(id+"F0.wireOp",EDGE,"E6"),sQuery(id+"F0.wireOp",EDGE,"E7"),sQuery(id+"F0.wireOp",EDGE,"E8"),sQuery(id+"F0.wireOp",EDGE,"E9"),subQ0,subQ1,sQuery(id+"F0.wireOp",EDGE,"E12"),sQuery(id+"F0.wireOp",EDGE,"E13"),sQuery(id+"F0.wireOp",EDGE,"E14"),sQuery(id+"F0.wireOp",EDGE,"E15"),sQuery(id+"F0.wireOp",EDGE,"E16"),sQuery(id+"F0.wireOp",EDGE,"E17.filletArc"),subQ2,subQ3,sQuery(id+"F0.wireOp",EDGE,"E26"),sQuery(id+"F0.wireOp",EDGE,"E27"),sQuery(id+"F0.wireOp",EDGE,"E28"),sQuery(id+"F0.wireOp",EDGE,"E29"),sQuery(id+"F0.wireOp",EDGE,"E30"),sQuery(id+"F0.wireOp",EDGE,"E31"),sQuery(id+"F0.wireOp",EDGE,"E32"),sQuery(id+"F0.wireOp",EDGE,"E33"),sQuery(id+"F0.wireOp",EDGE,"E34"),sQuery(id+"F0.wireOp",EDGE,"E35"),sQuery(id+"F0.wireOp",EDGE,"E37"),sQuery(id+"F0.wireOp",EDGE,"E39")])],"isStart":false})});}
            extrude(context, id + "F18", {"entities" : qUnion([Q0, Q1]), "operationType" : NewBodyOperationType.REMOVE, "endBound" : BoundingType.UP_TO_SURFACE, "oppositeDirection" : true, "endBoundEntityFace" : qUnion([Q2]), "depth" : 25 * mm});
        }
        {
            var Q0;
            Q0=makeQuery(id+"F18.boolean.opBoolean","COPY",EDGE,{"derivedFrom":makeQuery(id+"F18.opExtrude","SWEPT_EDGE",EDGE,{"disambiguationData":[OSD([sQuery(id+"F2.wireOp",EDGE,"E40.0"),sQuery(id+"F17.wireOp",EDGE,"E65")])]})});
            var Q1;
            Q1=makeQuery(id+"F18.boolean.opBoolean","COPY",EDGE,{"derivedFrom":makeQuery(id+"F18.opExtrude","SWEPT_EDGE",EDGE,{"disambiguationData":[OSD([sQuery(id+"F2.wireOp",EDGE,"E41.0"),sQuery(id+"F17.wireOp",EDGE,"E65")])]})});
            var Q2;
            Q2=makeQuery(id+"F18.boolean.opBoolean","COPY",EDGE,{"derivedFrom":makeQuery(id+"F18.opExtrude","SWEPT_EDGE",EDGE,{"disambiguationData":[OSD([sQuery(id+"F2.wireOp",EDGE,"E42.0"),sQuery(id+"F17.wireOp",EDGE,"E66")])]})});
            var Q3;
            Q3=makeQuery(id+"F18.boolean.opBoolean","COPY",EDGE,{"derivedFrom":makeQuery(id+"F18.opExtrude","SWEPT_EDGE",EDGE,{"disambiguationData":[OSD([sQuery(id+"F2.wireOp",EDGE,"E43.0"),sQuery(id+"F17.wireOp",EDGE,"E66")])]})});
            var Q4;
            Q4=makeQuery(id+"F3.opExtrude","SWEPT_EDGE",EDGE,{"disambiguationData":[OSD([sQuery(id+"F0.wireOp",EDGE,"E10"),sQuery(id+"F2.wireOp",EDGE,"E41.0")])]});
            var Q5;
            Q5=makeQuery(id+"F1.opExtrude","SWEPT_EDGE",EDGE,{"disambiguationData":[OSD([sQuery(id+"F0.wireOp",EDGE,"E10"),sQuery(id+"F0.wireOp",EDGE,"E11")])]});
            var Q6;
            Q6=makeQuery(id+"F3.opExtrude","SWEPT_EDGE",EDGE,{"disambiguationData":[OSD([sQuery(id+"F0.wireOp",EDGE,"E11"),sQuery(id+"F2.wireOp",EDGE,"E40.0")])]});
            var Q7;
            {var subQ0=sQuery(id+"F0.wireOp",EDGE,"E11");var subQ1=sQuery(id+"F0.wireOp",EDGE,"E12");Q7=makeQuery(id+"F3.boolean.opBoolean","MERGE",EDGE,{"derivedFrom":[makeQuery(id+"F1.opExtrude","SWEPT_EDGE",EDGE,{"disambiguationData":[OSD([subQ0,subQ1])]}),makeQuery(id+"F3.opExtrude","SWEPT_EDGE",EDGE,{"disambiguationData":[OSD([subQ0,subQ1])]})]});}
            var Q8;
            {var subQ0=sQuery(id+"F0.wireOp",EDGE,"E14");var subQ1=sQuery(id+"F0.wireOp",EDGE,"E15");Q8=makeQuery(id+"F3.boolean.opBoolean","MERGE",EDGE,{"derivedFrom":[makeQuery(id+"F1.opExtrude","SWEPT_EDGE",EDGE,{"disambiguationData":[OSD([subQ0,subQ1])]}),makeQuery(id+"F3.opExtrude","SWEPT_EDGE",EDGE,{"disambiguationData":[OSD([subQ0,subQ1])]})]});}
            var Q9;
            Q9=makeQuery(id+"F3.opExtrude","SWEPT_EDGE",EDGE,{"disambiguationData":[OSD([sQuery(id+"F0.wireOp",EDGE,"E15"),sQuery(id+"F2.wireOp",EDGE,"E42.0")])]});
            var Q10;
            Q10=makeQuery(id+"F1.opExtrude","SWEPT_EDGE",EDGE,{"disambiguationData":[OSD([sQuery(id+"F0.wireOp",EDGE,"E15"),sQuery(id+"F0.wireOp",EDGE,"E16")])]});
            var Q11;
            Q11=makeQuery(id+"F3.opExtrude","SWEPT_EDGE",EDGE,{"disambiguationData":[OSD([sQuery(id+"F0.wireOp",EDGE,"E16"),sQuery(id+"F2.wireOp",EDGE,"E43.0")])]});
            var Q12;
            {var subQ0=sQuery(id+"F0.wireOp",EDGE,"E28");var subQ1=sQuery(id+"F0.wireOp",EDGE,"E31");Q12=makeQuery(id+"F3.boolean.opBoolean","MERGE",EDGE,{"derivedFrom":[makeQuery(id+"F1.opExtrude","SWEPT_EDGE",EDGE,{"disambiguationData":[OSD([subQ0,subQ1])]}),makeQuery(id+"F3.opExtrude","SWEPT_EDGE",EDGE,{"disambiguationData":[OSD([subQ0,subQ1])]})]});}
            var Q13;
            {var subQ0=sQuery(id+"F0.wireOp",EDGE,"E28");var subQ1=sQuery(id+"F0.wireOp",EDGE,"E29");Q13=makeQuery(id+"F3.boolean.opBoolean","MERGE",EDGE,{"derivedFrom":[makeQuery(id+"F1.opExtrude","SWEPT_EDGE",EDGE,{"disambiguationData":[OSD([subQ0,subQ1])]}),makeQuery(id+"F3.opExtrude","SWEPT_EDGE",EDGE,{"disambiguationData":[OSD([subQ0,subQ1])]})]});}
            fillet(context, id + "F19", {"entities" : qUnion([Q0, Q1, Q2, Q3, Q4, Q5, Q6, Q7, Q8, Q9, Q10, Q11, Q12, Q13]), "radius" : 2 * mm, "tangentPropagation" : true, "allowEdgeOverflow" : false});
        }
        {
            var Q0;
            {var subQ0=sQuery(id+"F0.wireOp",EDGE,"E0.rect.bottom");var subQ1=sQuery(id+"F0.wireOp",EDGE,"E0.rect.top");var subQ2=sQuery(id+"F0.wireOp",EDGE,"E0.rect.left");var subQ3=sQuery(id+"F0.wireOp",EDGE,"E0.rect.right");var subQ4=sQuery(id+"F0.wireOp",EDGE,"E1");var subQ5=sQuery(id+"F0.wireOp",EDGE,"E2");var subQ6=sQuery(id+"F0.wireOp",EDGE,"E3");var subQ7=sQuery(id+"F0.wireOp",EDGE,"E4");var subQ8=sQuery(id+"F0.wireOp",EDGE,"E5");var subQ9=sQuery(id+"F0.wireOp",EDGE,"E6");var subQ10=sQuery(id+"F0.wireOp",EDGE,"E7");var subQ11=sQuery(id+"F0.wireOp",EDGE,"E8");var subQ12=sQuery(id+"F0.wireOp",EDGE,"E9");Q0=makeQuery(id+"F7.boolean.opBoolean","MERGE",FACE,{"derivedFrom":[makeQuery(id+"F1.opExtrude","CAP_FACE",FACE,{"disambiguationData":[OSD([subQ0,subQ1,subQ2,subQ3,subQ4,subQ5,subQ6,subQ7,subQ8,subQ9,subQ10,subQ11,subQ12,sQuery(id+"F0.wireOp",EDGE,"E10"),sQuery(id+"F0.wireOp",EDGE,"E11"),sQuery(id+"F0.wireOp",EDGE,"E12"),sQuery(id+"F0.wireOp",EDGE,"E13"),sQuery(id+"F0.wireOp",EDGE,"E14"),sQuery(id+"F0.wireOp",EDGE,"E15"),sQuery(id+"F0.wireOp",EDGE,"E16"),sQuery(id+"F0.wireOp",EDGE,"E17.filletArc"),sQuery(id+"F0.wireOp",EDGE,"E24"),sQuery(id+"F0.wireOp",EDGE,"E25"),sQuery(id+"F0.wireOp",EDGE,"E26"),sQuery(id+"F0.wireOp",EDGE,"E27"),sQuery(id+"F0.wireOp",EDGE,"E28"),sQuery(id+"F0.wireOp",EDGE,"E29"),sQuery(id+"F0.wireOp",EDGE,"E30"),sQuery(id+"F0.wireOp",EDGE,"E31"),sQuery(id+"F0.wireOp",EDGE,"E32"),sQuery(id+"F0.wireOp",EDGE,"E33"),sQuery(id+"F0.wireOp",EDGE,"E34"),sQuery(id+"F0.wireOp",EDGE,"E35"),sQuery(id+"F0.wireOp",EDGE,"E37"),sQuery(id+"F0.wireOp",EDGE,"E39")])],"isStart":true}),makeQuery(id+"F7.opExtrude","CAP_FACE",FACE,{"disambiguationData":[OSD([subQ0,subQ1,subQ2,subQ3,subQ4,subQ5,subQ6,subQ7,subQ8,subQ9,subQ10,subQ11,subQ12])],"isStart":true})]});}
            chamfer(context, id + "F20", {"entities" : qUnion([Q0]), "width" : 0.5 * mm, "tangentPropagation" : true});
        }
    });
